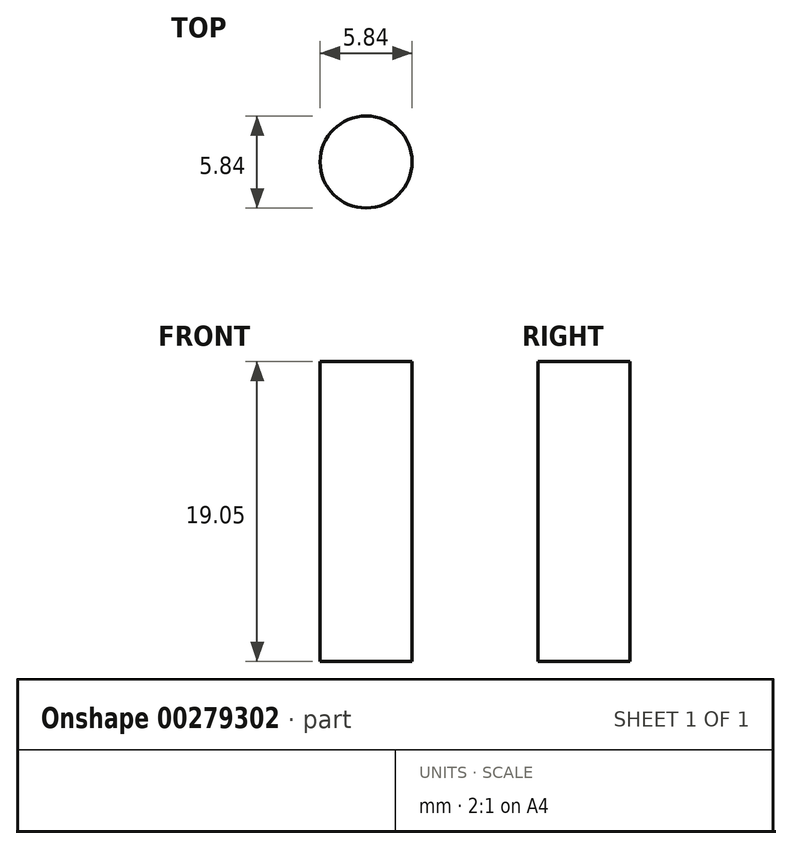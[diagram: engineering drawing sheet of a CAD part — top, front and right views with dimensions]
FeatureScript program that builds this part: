
annotation { "Feature Type Name" : "Feature", "Feature Type Description" : "" }
export const myFeature = defineFeature(function(context is Context, id is Id, definition is map)
    precondition{}
    {
        {
            var Q0;
            Q0=qCreatedBy(makeId("Top.planeOp"),FACE);
            var sketch = newSketch(context, id + "F0", { "sketchPlane" : qUnion([Q0])});
            skCircle(sketch, "E0", {"center": v(-24.86, 30.12) * mm, "radius": 2.92 * mm});
            skSolve(sketch);
        }
        {
            var Q0;
            Q0 = qSketchRegion(id + "F0", true);
            extrude(context, id + "F1", {"entities" : qUnion([Q0]), "flatOperationType" : FlatOperationType.REMOVE, "offsetDistance" : 25.4 * mm, "depth" : 19.05 * mm, "domain" : OperationDomain.MODEL});
        }
    });
